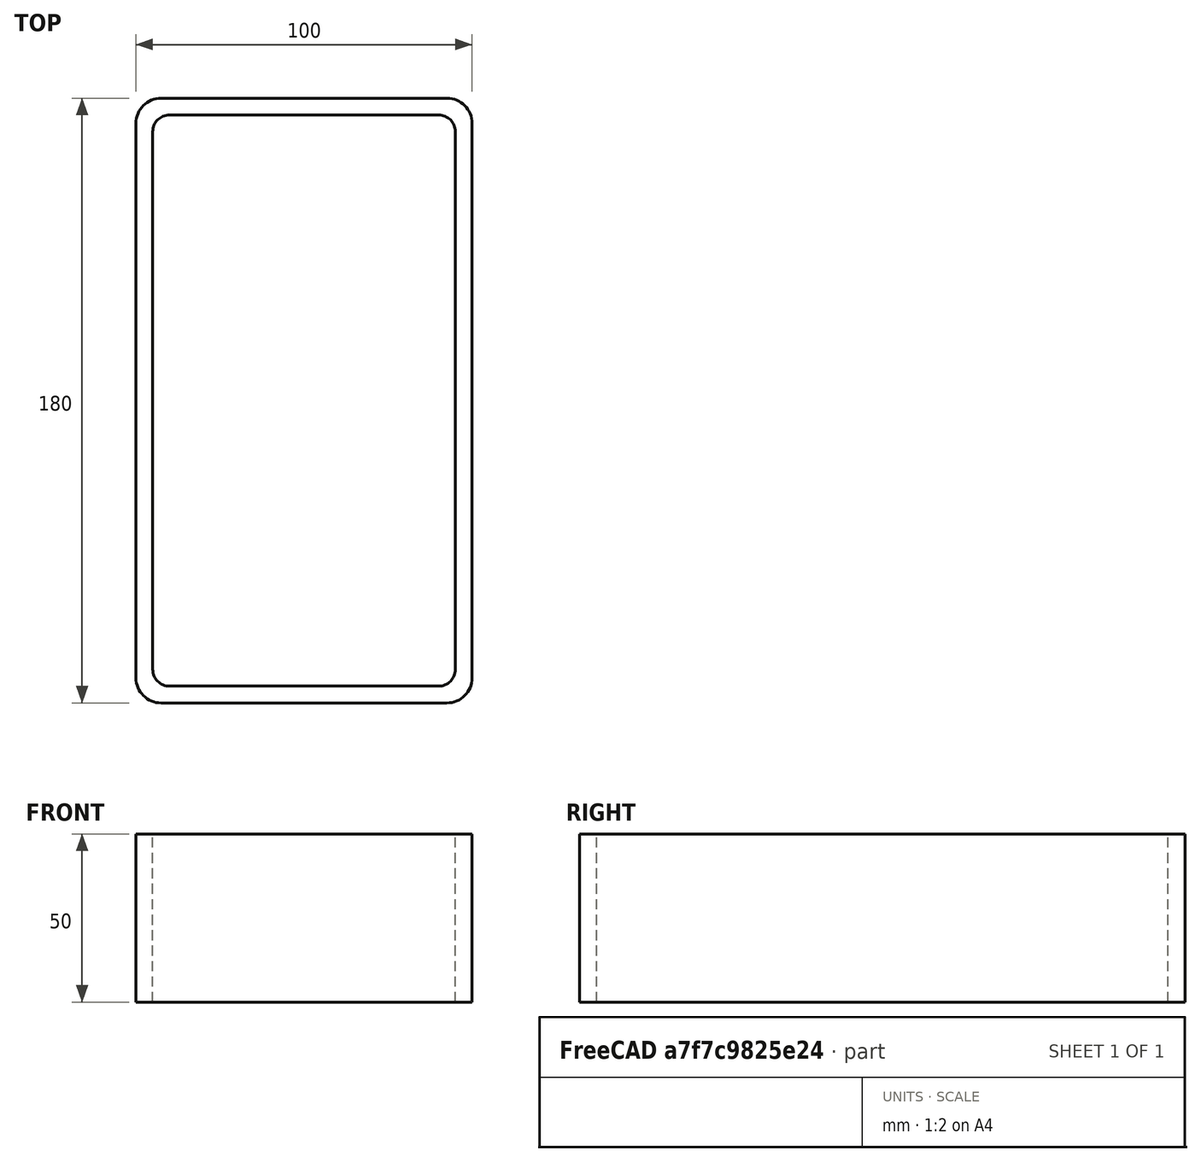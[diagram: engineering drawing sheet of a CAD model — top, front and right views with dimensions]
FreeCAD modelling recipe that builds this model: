
FCSTD DOCUMENT  (FreeCAD 0.15R4671 (Git))
Label: Rectangular hollow section 180x100x5 EN10219 S235JRH
License: All rights reserved
LicenseURL: http://en.wikipedia.org/wiki/All_rights_reserved
objects: Sketcher::SketchObject×1, Part::Extrusion×1
note: 2 computed .brp shape members not serialized (recipe doc carries the construction recipe); baked Part::Feature solids carry a one-line shape summary decoded from their .brp

FEATURE [Sketcher::SketchObject] Sketch
  sketch-geometry (16):
    g0: LineSegment StartX=-40 StartY=85 StartZ=0 EndX=40 EndY=85 EndZ=0
    g1: LineSegment StartX=45 StartY=80 StartZ=0 EndX=45 EndY=-80 EndZ=0
    g2: LineSegment StartX=40 StartY=-85 StartZ=0 EndX=-40 EndY=-85 EndZ=0
    g3: LineSegment StartX=-45 StartY=-80 StartZ=0 EndX=-45 EndY=80 EndZ=0
    g4: LineSegment StartX=-42.5 StartY=90 StartZ=0 EndX=42.5 EndY=90 EndZ=0
    g5: LineSegment StartX=50 StartY=82.5 StartZ=0 EndX=50 EndY=-82.5 EndZ=0
    g6: LineSegment StartX=42.5 StartY=-90 StartZ=0 EndX=-42.5 EndY=-90 EndZ=0
    g7: LineSegment StartX=-50 StartY=-82.5 StartZ=0 EndX=-50 EndY=82.5 EndZ=0
    g8: ArcOfCircle CenterX=-40 CenterY=80 CenterZ=0 NormalX=0 NormalY=0 NormalZ=1 Radius=5 StartAngle=1.5708 EndAngle=3.14159
    g9: ArcOfCircle CenterX=40 CenterY=80 CenterZ=0 NormalX=0 NormalY=0 NormalZ=1 Radius=5 StartAngle=0 EndAngle=1.5708
    g10: ArcOfCircle CenterX=40 CenterY=-80 CenterZ=0 NormalX=0 NormalY=0 NormalZ=1 Radius=5 StartAngle=4.71239 EndAngle=6.28319
    g11: ArcOfCircle CenterX=-40 CenterY=-80 CenterZ=0 NormalX=0 NormalY=0 NormalZ=1 Radius=5 StartAngle=3.14159 EndAngle=4.71239
    g12: ArcOfCircle CenterX=42.5 CenterY=82.5 CenterZ=0 NormalX=0 NormalY=0 NormalZ=1 Radius=7.5 StartAngle=0 EndAngle=1.5708
    g13: ArcOfCircle CenterX=42.5 CenterY=-82.5 CenterZ=0 NormalX=0 NormalY=0 NormalZ=1 Radius=7.5 StartAngle=4.71239 EndAngle=6.28319
    g14: ArcOfCircle CenterX=-42.5 CenterY=-82.5 CenterZ=0 NormalX=0 NormalY=0 NormalZ=1 Radius=7.5 StartAngle=3.14159 EndAngle=4.71239
    g15: ArcOfCircle CenterX=-42.5 CenterY=82.5 CenterZ=0 NormalX=0 NormalY=0 NormalZ=1 Radius=7.5 StartAngle=1.5708 EndAngle=3.14159
  constraints (36):
    c: Horizontal(g2)
    c: Vertical(g3)
    c: Horizontal(g6)
    c: Vertical(g7)
    c: Tangent(g3,g8) = 1.5708
    c: Tangent(g0,g8) = 1.5708
    c: Tangent(g0,g9) = 1.5708
    c: Tangent(g1,g9) = 1.5708
    c: Tangent(g1,g10) = 1.5708
    c: Tangent(g2,g10) = 1.5708
    c: Tangent(g2,g11) = 1.5708
    c: Tangent(g3,g11) = 1.5708
    c: Tangent(g4,g12) = 1.5708
    c: Tangent(g5,g12) = 1.5708
    c: Tangent(g5,g13) = 1.5708
    c: Tangent(g6,g13) = 1.5708
    c: Tangent(g6,g14) = 1.5708
    c: Tangent(g7,g14) = 1.5708
    c: Tangent(g7,g15) = 1.5708
    c: Tangent(g4,g15) = 1.5708
    c: Equal(g9,g8)
    c: Equal(g9,g11)
    c: Equal(g9,g10)
    c: Equal(g12,g15)
    c: Equal(g12,g14)
    c: Equal(g12,g13)
    c: Symmetric(g4,g6,g-1)
    c: Symmetric(g7,g5,g-2)
    c: DistanceY(g4,g6) = -180
    c: DistanceX(g7,g5) = 100
    c: Symmetric(g3,g1,g-2)
    c: Symmetric(g0,g2,g-1)
    c: DistanceY(g0,g4) = 5
    c: DistanceX(g5,g1) = -5
    c: Radius(g9) = 5
    c: Radius(g12) = 7.5
FEATURE [Part::Extrusion] Extrude  label="Rectangular hollow section 180x100x5 EN10219 S235JRH"
  Base = -> Sketch
  Dir = (0,0,50)
  Solid = true
